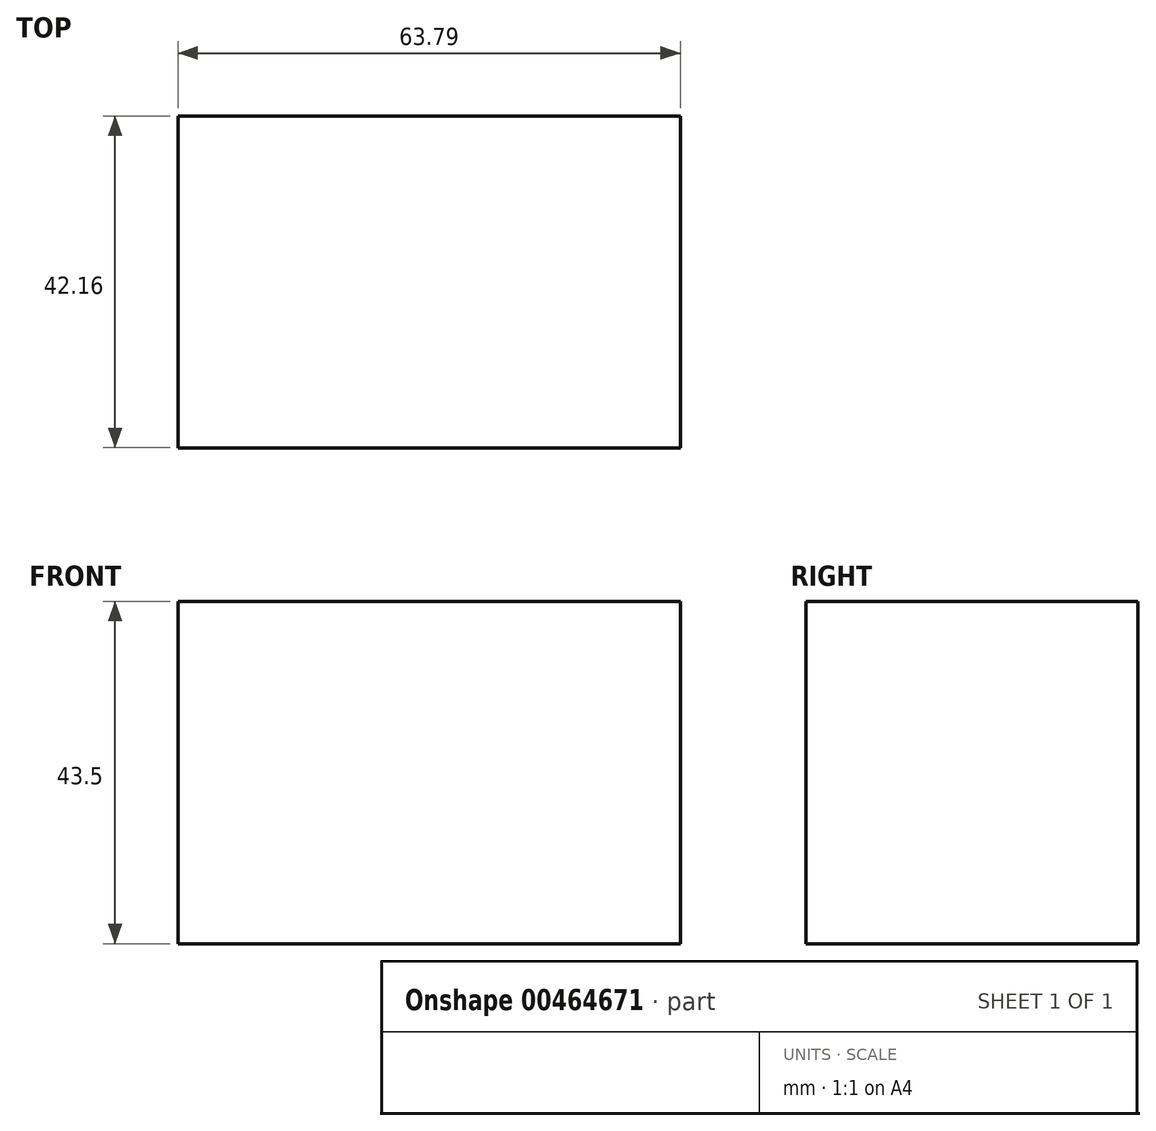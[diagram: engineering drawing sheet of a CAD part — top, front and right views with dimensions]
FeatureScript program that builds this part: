
annotation { "Feature Type Name" : "Feature", "Feature Type Description" : "" }
export const myFeature = defineFeature(function(context is Context, id is Id, definition is map)
    precondition{}
    {
        {
            var Q0;
            Q0=qCreatedBy(makeId("Front.planeOp"),FACE);
            var sketch = newSketch(context, id + "F0", { "sketchPlane" : qUnion([Q0])});
            skLineSegment(sketch, "E0.bottom", {"start": v(-59.69, 14.46) * mm, "end": v(4.1, 14.46) * mm});
            skLineSegment(sketch, "E0.top", {"start": v(-59.69, -29.04) * mm, "end": v(4.1, -29.04) * mm});
            skLineSegment(sketch, "E0.left", {"start": v(-59.69, 14.46) * mm, "end": v(-59.69, -29.04) * mm});
            skLineSegment(sketch, "E0.right", {"start": v(4.1, 14.46) * mm, "end": v(4.1, -29.04) * mm});
            skSolve(sketch);
        }
        {
            var Q0;
            Q0 = qSketchRegion(id + "F0", true);
            extrude(context, id + "F1", {"entities" : qUnion([Q0]), "depth" : 42.16 * mm});
        }
    });
